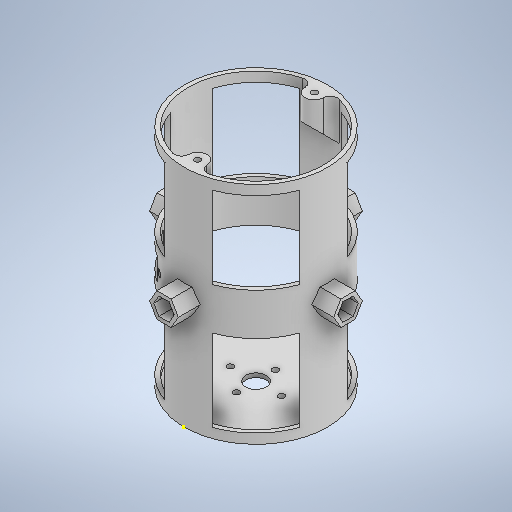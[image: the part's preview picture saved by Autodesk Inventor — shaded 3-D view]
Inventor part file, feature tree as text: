
AUTODESK INVENTOR PART (.ipt)
format: ipt  version: 2025.3 (Build 293356000, 356)  size: 537,600 bytes
history: native  units: in
note: dims shown in document units (in); Inventor stores cm internally (conversion verified against a paired STEP export)
features: sketch x9, extrude x8, mirror x5, fillet x4, plane x3, projected_geometry x2, shell x1, boolean_combine x1
ambient origin geometry x8: Origin, YZ Plane, XZ Plane, XY Plane, X Axis, Y Axis, Z Axis, Center Point
bodies: Solid1 (feature_tree), Solid2 (feature_tree)
feature tree (33):
  extrude  "Extrusion1"  Depth=0.0787in TaperAngle=0.0deg
  shell  "Shell1"  Thickness=0.0787in
  extrude  "Extrusion2"  Depth=0.1181in
  extrude  "Extrusion3"  Depth=0.3937in TaperAngle=0.0deg
  mirror  "Mirror2"
  boolean_combine  "Combine2"
  extrude  "Extrusion4"  Depth=0.122in
  plane  "Work Plane1"
  sketch  "Sketch7"  dims[d37=0.122in d38=0.122in]
  extrude  "Extrusion5"  Depth=0.122in
  plane  "Work Plane2"
  plane  "Work Plane3"
  extrude  "Extrusion7"  Depth=0.9843in
  fillet  "Face Fillet13"
  fillet  "Face Fillet14"
  fillet  "Face Fillet15"
  fillet  "Face Fillet16"
  extrude  "Extrusion10"  Depth=0.4921in
  extrude  "Extrusion9"  Depth=1.378in
  mirror  "Mirror5"
  mirror  "Mirror6"
  mirror  "Mirror7"
  mirror  "Mirror8"
  sketch  "Sketch1"  dims[d0=2.7559in d1=4.3307in d2=0.0in d3=0.0787in]
  sketch  "Sketch4"  dims[d15=0.3543in d16=0.1181in]
  sketch  "Sketch5"  dims[d17=0.7874in d18=0.0in d22=0.3937in d23=0.0in]
  sketch  "Sketch6"  dims[d35=0.122in d36=0.122in]
  sketch  "Sketch8"  dims[d39=0.748in d40=0.9843in]
  sketch  "Sketch10"  dims[d41=0.374in d42=0.4921in]
  sketch  "Sketch12"  dims[d43=0.3937in d44=0.0in d45=1.378in]
  projected_geometry  "Projected Loop5"
  projected_geometry  "Projected Loop6"
  sketch  "Sketch13"  dims[d46=2.1654in d49=0.3937in d50=0.0in d53=1.378in d54=0.4331in d55=0.6102in d56=0.1969in d57=0.1181in d58=0.0in d59=0.0in d60=45.0deg d61=0.1346in d62=0.1346in d63=0.1346in d64=0.1346in d65=0.3937in d66=0.5512in d67=2.1654in d68=2.1654in d69=1.5748in d71=45.0deg d72=0.3937in d73=0.3937in d76=0.3937in d77=0.0in d78=1.5748in d79=1.1811in d80=0.187in d81=1.5748in d82=1.1811in d83=0.187in d84=0.3937in d85=0.0in d74=0.0197in d75=0.0344in]
